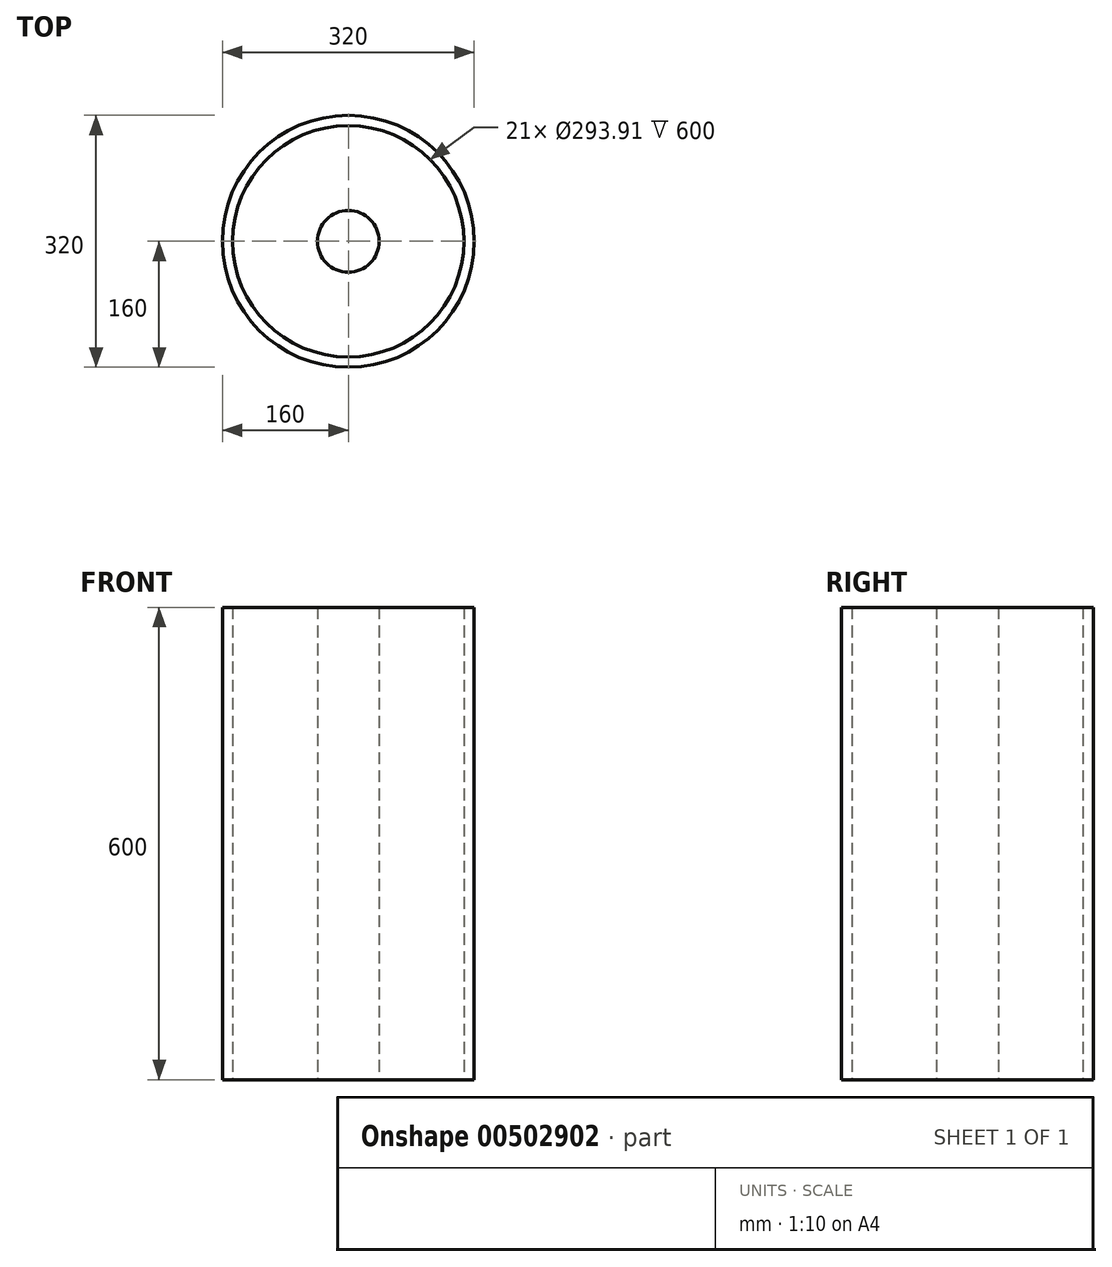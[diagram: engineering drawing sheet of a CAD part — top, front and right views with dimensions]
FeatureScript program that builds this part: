
annotation { "Feature Type Name" : "Feature", "Feature Type Description" : "" }
export const myFeature = defineFeature(function(context is Context, id is Id, definition is map)
    precondition{}
    {
        {
            var Q0;
            Q0=qCreatedBy(makeId("Top.planeOp"),FACE);
            var sketch = newSketch(context, id + "F0", { "sketchPlane" : qUnion([Q0])});
            skCircle(sketch, "E0", {"center": v(0, 0) * mm, "radius": 39.19 * mm});
            skCircle(sketch, "E1", {"center": v(0, 0) * mm, "radius": 146.95 * mm});
            skCircle(sketch, "E2", {"center": v(0, 0) * mm, "radius": 160 * mm});
            skSolve(sketch);
        }
        {
            var Q0;
            Q0=makeQuery(id+"F0.imprint","IMPRINT",FACE,{"disambiguationData":[TD([[makeQuery(id+"F0.imprint","IMPRINT",EDGE,{"derivedFrom":sQuery(id+"F0.wireOp",EDGE,"E0")}),1.0]])]});
            extrude(context, id + "F1", {"entities" : qUnion([Q0]), "depth" : 600 * mm});
        }
        {
            var Q0;
            Q0 = qSketchRegion(id + "F0", true);
            extrude(context, id + "F2", {"entities" : qUnion([Q0]), "depth" : 600 * mm});
        }
    });
